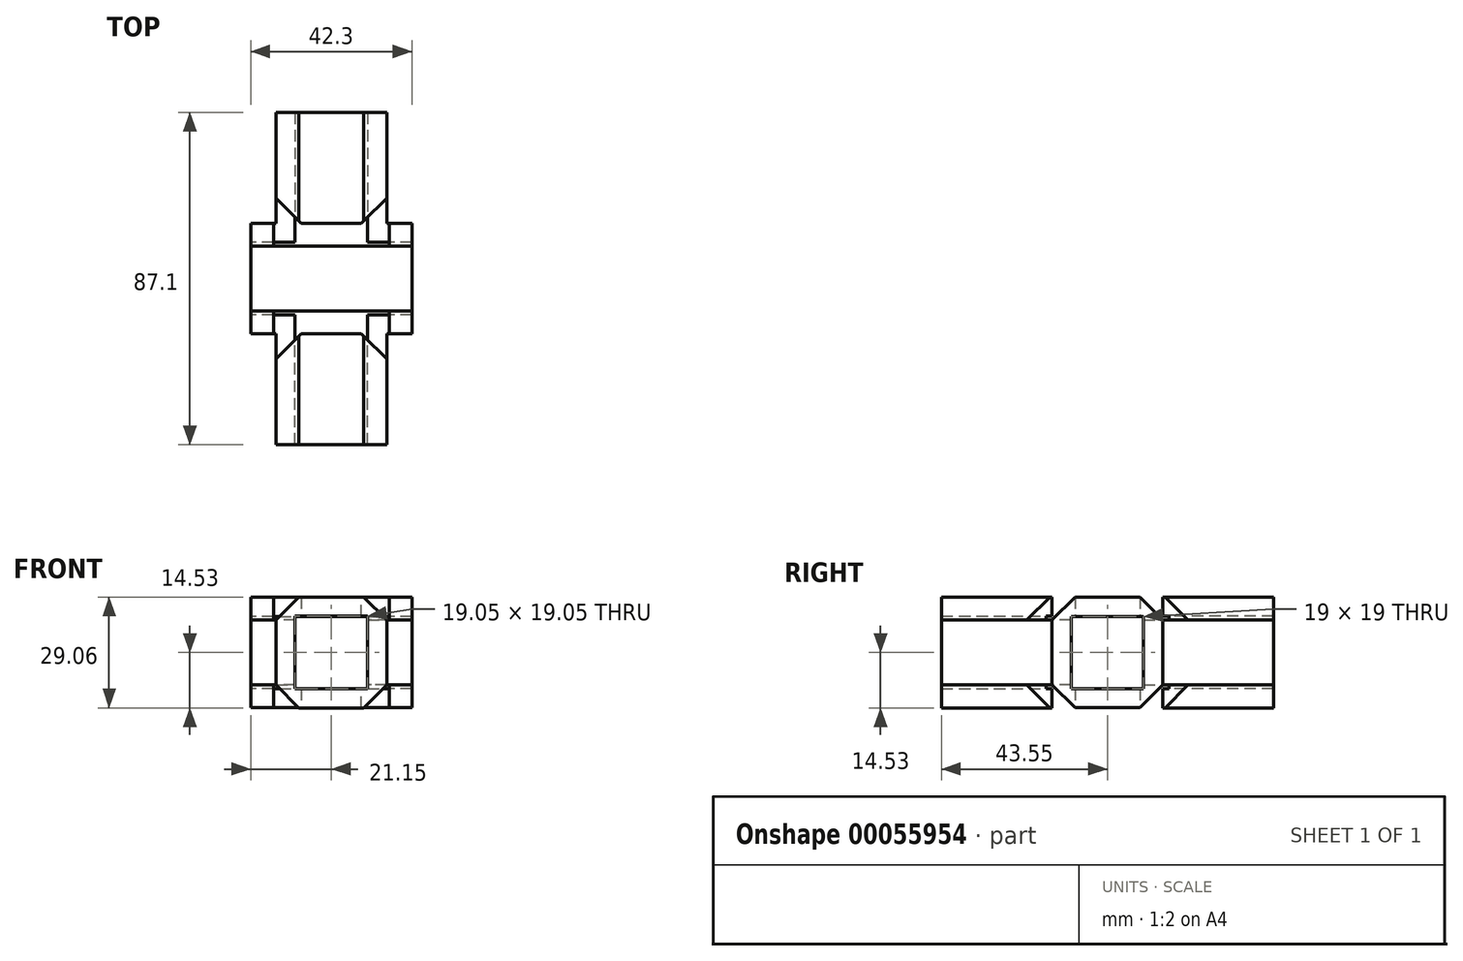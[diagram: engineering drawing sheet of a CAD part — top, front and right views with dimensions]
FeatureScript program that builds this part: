
annotation { "Feature Type Name" : "Feature", "Feature Type Description" : "" }
export const myFeature = defineFeature(function(context is Context, id is Id, definition is map)
    precondition{}
    {
        {
            var Q0;
            Q0=qCreatedBy(makeId("Right.planeOp"),FACE);
            var sketch = newSketch(context, id + "F0", { "sketchPlane" : qUnion([Q0])});
            skLineSegment(sketch, "E0.rect.bottom", {"start": v(9.5, 9.5) * mm, "end": v(0, 9.5) * mm});
            skLineSegment(sketch, "E0.rect.top", {"start": v(9.5, -9.5) * mm, "end": v(0, -9.5) * mm});
            skLineSegment(sketch, "E0.rect.left", {"start": v(9.5, 9.5) * mm, "end": v(9.5, -9.5) * mm});
            skPoint(sketch, "E0.rect.middle", {"position": v(0, 0) * mm});
            skLineSegment(sketch, "E1.rect.bottom", {"start": v(14.5, 14.5) * mm, "end": v(0, 14.5) * mm});
            skLineSegment(sketch, "E1.rect.top", {"start": v(14.5, -14.5) * mm, "end": v(0, -14.5) * mm});
            skLineSegment(sketch, "E1.rect.left", {"start": v(14.5, 14.5) * mm, "end": v(14.5, -14.5) * mm});
            skLineSegment(sketch, "E2", {"start": v(0, 9.5) * mm, "end": v(0, 14.5) * mm});
            skLineSegment(sketch, "E3", {"start": v(0, -9.5) * mm, "end": v(0, -14.5) * mm});
            skSolve(sketch);
        }
        {
            var Q0;
            Q0=makeQuery(id+"F0.imprint","IMPRINT",FACE,{"disambiguationData":[TD([[makeQuery(id+"F0.imprint","IMPRINT",EDGE,{"derivedFrom":sQuery(id+"F0.wireOp",EDGE,"5346ee42-6b44-4ab4-b06a-5ea702be0697.bottom")}),1.0]])]});
            var Q1;
            Q1=makeQuery(id+"F0.imprint","IMPRINT",FACE,{"disambiguationData":[TD([[makeQuery(id+"F0.imprint","IMPRINT",EDGE,{"derivedFrom":sQuery(id+"F0.wireOp",EDGE,"9599e187-f427-41b1-8912-62db417e26b9.bottom")}),1.0]])]});
            var Q2;
            Q2=makeQuery(id+"F0.imprint","IMPRINT",FACE,{"disambiguationData":[TD([[makeQuery(id+"F0.imprint","IMPRINT",EDGE,{"derivedFrom":sQuery(id+"F0.wireOp",EDGE,"E0.rect.bottom")}),-1.0]])]});
            extrude(context, id + "F1", {"entities" : qUnion([Q0, Q1, Q2]), "depth" : 42.3 * mm});
        }
        {
            var Q0;
            Q0=makeQuery(id+"F1.opExtrude","SWEPT_FACE",FACE,{"disambiguationData":[OSD([sQuery(id+"F0.wireOp",EDGE,"E1.rect.left")])]});
            var sketch = newSketch(context, id + "F2", { "sketchPlane" : qUnion([Q0])});
            skLineSegment(sketch, "E4.bottom", {"start": v(-42.3, 14.5) * mm, "end": v(-36.3, 14.5) * mm, "construction": true});
            skLineSegment(sketch, "E4.top", {"start": v(-42.3, 8.5) * mm, "end": v(-36.3, 8.5) * mm, "construction": true});
            skLineSegment(sketch, "E4.left", {"start": v(-42.3, 14.5) * mm, "end": v(-42.3, 8.5) * mm, "construction": true});
            skLineSegment(sketch, "E4.right", {"start": v(-36.3, 14.5) * mm, "end": v(-36.3, 8.5) * mm, "construction": true});
            skLineSegment(sketch, "E5.bottom", {"start": v(0, 14.5) * mm, "end": v(-6, 14.5) * mm, "construction": true});
            skLineSegment(sketch, "E5.top", {"start": v(0, 8.5) * mm, "end": v(-6, 8.5) * mm, "construction": true});
            skLineSegment(sketch, "E5.left", {"start": v(0, 14.5) * mm, "end": v(0, 8.5) * mm, "construction": true});
            skLineSegment(sketch, "E5.right", {"start": v(-6, 14.5) * mm, "end": v(-6, 8.5) * mm, "construction": true});
            skLineSegment(sketch, "E6.bottom", {"start": v(0, -14.5) * mm, "end": v(-6, -14.5) * mm, "construction": true});
            skLineSegment(sketch, "E6.top", {"start": v(0, -8.5) * mm, "end": v(-6, -8.5) * mm, "construction": true});
            skLineSegment(sketch, "E6.left", {"start": v(0, -14.5) * mm, "end": v(0, -8.5) * mm, "construction": true});
            skLineSegment(sketch, "E6.right", {"start": v(-6, -14.5) * mm, "end": v(-6, -8.5) * mm, "construction": true});
            skLineSegment(sketch, "E7.bottom", {"start": v(-42.3, -14.5) * mm, "end": v(-36.3, -14.5) * mm, "construction": true});
            skLineSegment(sketch, "E7.top", {"start": v(-42.3, -8.5) * mm, "end": v(-36.3, -8.5) * mm, "construction": true});
            skLineSegment(sketch, "E7.left", {"start": v(-42.3, -14.5) * mm, "end": v(-42.3, -8.5) * mm, "construction": true});
            skLineSegment(sketch, "E7.right", {"start": v(-36.3, -14.5) * mm, "end": v(-36.3, -8.5) * mm, "construction": true});
            skLineSegment(sketch, "E8.bottom", {"start": v(-36.3, 14.5) * mm, "end": v(-6, 14.5) * mm});
            skLineSegment(sketch, "E8.top", {"start": v(-36.3, 8.5) * mm, "end": v(-6, 8.5) * mm});
            skLineSegment(sketch, "E8.left", {"start": v(-36.3, 14.5) * mm, "end": v(-36.3, 8.5) * mm});
            skLineSegment(sketch, "E8.right", {"start": v(-6, 14.5) * mm, "end": v(-6, 8.5) * mm});
            skLineSegment(sketch, "E9.bottom", {"start": v(-36.3, -8.5) * mm, "end": v(-6, -8.5) * mm});
            skLineSegment(sketch, "E9.top", {"start": v(-36.3, -14.5) * mm, "end": v(-6, -14.5) * mm});
            skLineSegment(sketch, "E9.left", {"start": v(-36.3, -8.5) * mm, "end": v(-36.3, -14.5) * mm});
            skLineSegment(sketch, "E9.right", {"start": v(-6, -8.5) * mm, "end": v(-6, -14.5) * mm});
            skSolve(sketch);
        }
        {
            var Q0;
            Q0=makeQuery(id+"F2.imprint","IMPRINT",FACE,{"disambiguationData":[TD([[makeQuery(id+"F2.imprint","IMPRINT",EDGE,{"derivedFrom":sQuery(id+"F2.wireOp",EDGE,"E8.bottom")}),-1.0]])]});
            var Q1;
            Q1=makeQuery(id+"F2.imprint","IMPRINT",FACE,{"disambiguationData":[TD([[makeQuery(id+"F2.imprint","IMPRINT",EDGE,{"derivedFrom":sQuery(id+"F2.wireOp",EDGE,"E9.bottom")}),-1.0]])]});
            extrude(context, id + "F3", {"entities" : qUnion([Q0, Q1]), "operationType" : NewBodyOperationType.REMOVE, "oppositeDirection" : true, "depth" : 6 * mm});
        }
        {
            var Q0;
            {var subQ0=sQuery(id+"F0.wireOp",EDGE,"E1.rect.left");var subQ1=sQuery(id+"F0.wireOp",EDGE,"E1.rect.top");Q0=makeQuery(id+"F3.boolean.opBoolean","SPLIT",EDGE,{"disambiguationData":[TD([makeQuery(id+"F3.opExtrude","SWEPT_FACE",FACE,{"disambiguationData":[OSD([sQuery(id+"F2.wireOp",EDGE,"E9.right")])]})])],"derivedFrom":makeQuery(id+"F1.opExtrude","SWEPT_EDGE",EDGE,{"disambiguationData":[OSD([subQ1,subQ0])]})});}
            var Q1;
            {var subQ0=sQuery(id+"F0.wireOp",EDGE,"E1.rect.left");var subQ1=sQuery(id+"F0.wireOp",EDGE,"E1.rect.top");Q1=makeQuery(id+"F3.boolean.opBoolean","SPLIT",EDGE,{"disambiguationData":[TD([makeQuery(id+"F3.opExtrude","SWEPT_FACE",FACE,{"disambiguationData":[OSD([sQuery(id+"F2.wireOp",EDGE,"E9.left")])]})])],"derivedFrom":makeQuery(id+"F1.opExtrude","SWEPT_EDGE",EDGE,{"disambiguationData":[OSD([subQ1,subQ0])]})});}
            var Q2;
            {var subQ0=sQuery(id+"F0.wireOp",EDGE,"E1.rect.left");var subQ1=sQuery(id+"F0.wireOp",EDGE,"E1.rect.bottom");Q2=makeQuery(id+"F3.boolean.opBoolean","SPLIT",EDGE,{"disambiguationData":[TD([makeQuery(id+"F3.opExtrude","SWEPT_FACE",FACE,{"disambiguationData":[OSD([sQuery(id+"F2.wireOp",EDGE,"E8.left")])]})])],"derivedFrom":makeQuery(id+"F1.opExtrude","SWEPT_EDGE",EDGE,{"disambiguationData":[OSD([subQ1,subQ0])]})});}
            var Q3;
            {var subQ0=sQuery(id+"F0.wireOp",EDGE,"E1.rect.left");var subQ1=sQuery(id+"F0.wireOp",EDGE,"E1.rect.bottom");Q3=makeQuery(id+"F3.boolean.opBoolean","SPLIT",EDGE,{"disambiguationData":[TD([makeQuery(id+"F3.opExtrude","SWEPT_FACE",FACE,{"disambiguationData":[OSD([sQuery(id+"F2.wireOp",EDGE,"E8.right")])]})])],"derivedFrom":makeQuery(id+"F1.opExtrude","SWEPT_EDGE",EDGE,{"disambiguationData":[OSD([subQ1,subQ0])]})});}
            chamfer(context, id + "F4", {"entities" : qUnion([Q0, Q1, Q2, Q3]), "width" : 6 * mm, "tangentPropagation" : true});
        }
        {
            var Q0;
            Q0=makeQuery(id+"F1.opExtrude","SWEPT_FACE",FACE,{"disambiguationData":[OSD([sQuery(id+"F0.wireOp",EDGE,"E1.rect.left")])]});
            var sketch = newSketch(context, id + "F5", { "sketchPlane" : qUnion([Q0])});
            skLineSegment(sketch, "E10", {"start": v(-21.15, 9.5) * mm, "end": v(-21.15, -9.5) * mm, "construction": true});
            skLineSegment(sketch, "E11.rect.bottom", {"start": v(-11.62, 9.53) * mm, "end": v(-30.67, 9.53) * mm});
            skLineSegment(sketch, "E11.rect.top", {"start": v(-11.62, -9.52) * mm, "end": v(-30.67, -9.52) * mm});
            skLineSegment(sketch, "E11.rect.left", {"start": v(-11.62, 9.53) * mm, "end": v(-11.62, -9.52) * mm});
            skLineSegment(sketch, "E11.rect.right", {"start": v(-30.67, 9.53) * mm, "end": v(-30.67, -9.52) * mm});
            skPoint(sketch, "E11.rect.middle", {"position": v(-21.15, 0) * mm});
            skLineSegment(sketch, "E12.rect.bottom", {"start": v(-6.62, 14.53) * mm, "end": v(-35.67, 14.53) * mm});
            skLineSegment(sketch, "E12.rect.top", {"start": v(-6.62, -14.52) * mm, "end": v(-35.67, -14.52) * mm});
            skLineSegment(sketch, "E12.rect.left", {"start": v(-6.62, 14.53) * mm, "end": v(-6.62, -14.52) * mm});
            skLineSegment(sketch, "E12.rect.right", {"start": v(-35.67, 14.53) * mm, "end": v(-35.67, -14.53) * mm});
            skSolve(sketch);
        }
        {
            var Q0;
            {var subQ0=sQuery(id+"F5.wireOp",EDGE,"E11.rect.right");var subQ1=makeQuery(id+"F3.boolean.opBoolean","COPY",EDGE,{"derivedFrom":makeQuery(id+"F3.opExtrude","CAP_EDGE",EDGE,{"disambiguationData":[OSD([sQuery(id+"F2.wireOp",EDGE,"E8.top")])],"isStart":true})});var subQ2=makeQuery(id+"F5.imprint","INTERSECT",VERTEX,{"derivedFrom":[subQ1,subQ0]});Q0=makeQuery(id+"F5.imprint","IMPRINT",FACE,{"disambiguationData":[TD([[makeQuery(id+"F5.imprint","IMPRINT",EDGE,{"disambiguationData":[TD([[subQ2,-1.0]])],"derivedFrom":subQ0}),-1.0]])]});}
            var Q1;
            {var subQ0=sQuery(id+"F5.wireOp",EDGE,"E11.rect.left");var subQ1=makeQuery(id+"F3.boolean.opBoolean","COPY",EDGE,{"derivedFrom":makeQuery(id+"F3.opExtrude","CAP_EDGE",EDGE,{"disambiguationData":[OSD([sQuery(id+"F2.wireOp",EDGE,"E8.top")])],"isStart":true})});var subQ2=makeQuery(id+"F5.imprint","INTERSECT",VERTEX,{"derivedFrom":[subQ1,subQ0]});Q1=makeQuery(id+"F5.imprint","IMPRINT",FACE,{"disambiguationData":[TD([[makeQuery(id+"F5.imprint","IMPRINT",EDGE,{"disambiguationData":[TD([[subQ2,-1.0]])],"derivedFrom":subQ0}),1.0]])]});}
            var Q2;
            {var subQ1=sQuery(id+"F5.wireOp",EDGE,"E11.rect.bottom");Q2=makeQuery(id+"F5.imprint","IMPRINT",FACE,{"disambiguationData":[TD([[makeQuery(id+"F5.imprint","IMPRINT",EDGE,{"derivedFrom":subQ1}),-1.0]])]});}
            var Q3;
            {var subQ1=sQuery(id+"F5.wireOp",EDGE,"E11.rect.top");Q3=makeQuery(id+"F5.imprint","IMPRINT",FACE,{"disambiguationData":[TD([[makeQuery(id+"F5.imprint","IMPRINT",EDGE,{"derivedFrom":subQ1}),1.0]])]});}
            extrude(context, id + "F6", {"entities" : qUnion([Q0, Q1, Q2, Q3]), "operationType" : NewBodyOperationType.ADD, "depth" : 29.05 * mm});
        }
        {
            var Q0;
            {var subQ0=sQuery(id+"F5.wireOp",EDGE,"E11.rect.left");Q0=makeQuery(id+"F6.boolean.opBoolean","SPLIT",FACE,{"disambiguationData":[TD([makeQuery(id+"F6.opExtrude","SWEPT_FACE",FACE,{"disambiguationData":[OSD([subQ0])]})])],"derivedFrom":makeQuery(id+"F1.opExtrude","SWEPT_FACE",FACE,{"disambiguationData":[OSD([sQuery(id+"F0.wireOp",EDGE,"E1.rect.left")])]})});}
            extrude(context, id + "F7", {"entities" : qUnion([Q0]), "operationType" : NewBodyOperationType.REMOVE, "endBound" : BoundingType.UP_TO_NEXT, "oppositeDirection" : true, "depth" : 25 * mm});
        }
        {
            var Q0;
            {var subQ0=sQuery(id+"F5.wireOp",EDGE,"E12.rect.right");Q0=makeQuery(id+"F6.boolean.opBoolean","SPLIT",EDGE,{"disambiguationData":[topologyDisambiguationEdgeConnected([makeQuery(id+"F1.opExtrude","SWEPT_FACE",FACE,{"disambiguationData":[OSD([sQuery(id+"F0.wireOp",EDGE,"E1.rect.left")])]}),makeQuery(id+"F6.opExtrude","SWEPT_FACE",FACE,{"disambiguationData":[OSD([subQ0])]})])],"derivedFrom":makeQuery(id+"F6.opExtrude","CAP_EDGE",EDGE,{"disambiguationData":[OSD([subQ0])],"isStart":true})});}
            var Q1;
            {var subQ0=sQuery(id+"F5.wireOp",EDGE,"E12.rect.left");Q1=makeQuery(id+"F6.boolean.opBoolean","SPLIT",EDGE,{"disambiguationData":[topologyDisambiguationEdgeConnected([makeQuery(id+"F1.opExtrude","SWEPT_FACE",FACE,{"disambiguationData":[OSD([sQuery(id+"F0.wireOp",EDGE,"E1.rect.left")])]}),makeQuery(id+"F6.opExtrude","SWEPT_FACE",FACE,{"disambiguationData":[OSD([subQ0])]})])],"derivedFrom":makeQuery(id+"F6.opExtrude","CAP_EDGE",EDGE,{"disambiguationData":[OSD([subQ0])],"isStart":true})});}
            chamfer(context, id + "F8", {"entities" : qUnion([Q0, Q1]), "width" : 6.62 * mm, "tangentPropagation" : true});
        }
        {
            var Q0;
            Q0=makeQuery(id+"F6.opExtrude","SWEPT_EDGE",EDGE,{"disambiguationData":[OSD([sQuery(id+"F5.wireOp",EDGE,"E12.rect.bottom"),sQuery(id+"F5.wireOp",EDGE,"E12.rect.left")])]});
            var Q1;
            Q1=makeQuery(id+"F6.opExtrude","SWEPT_EDGE",EDGE,{"disambiguationData":[OSD([sQuery(id+"F5.wireOp",EDGE,"E12.rect.bottom"),sQuery(id+"F5.wireOp",EDGE,"E12.rect.right")])]});
            var Q2;
            Q2=makeQuery(id+"F6.opExtrude","SWEPT_EDGE",EDGE,{"disambiguationData":[OSD([sQuery(id+"F5.wireOp",EDGE,"E12.rect.top"),sQuery(id+"F5.wireOp",EDGE,"E12.rect.right")])]});
            var Q3;
            Q3=makeQuery(id+"F6.opExtrude","SWEPT_EDGE",EDGE,{"disambiguationData":[OSD([sQuery(id+"F5.wireOp",EDGE,"E12.rect.top"),sQuery(id+"F5.wireOp",EDGE,"E12.rect.left")])]});
            chamfer(context, id + "F9", {"entities" : qUnion([Q0, Q1, Q2, Q3]), "width" : 6 * mm, "tangentPropagation" : true});
        }
        {
            var Q0;
            Q0=makeQuery(id+"F1.opExtrude","SWEPT_FACE",FACE,{"disambiguationData":[OSD([sQuery(id+"F0.wireOp",EDGE,"E0.rect.top")])]});
            var sketch = newSketch(context, id + "F10", { "sketchPlane" : qUnion([Q0])});
            skLineSegment(sketch, "E13", {"start": v(6, 9.5) * mm, "end": v(36.3, 9.5) * mm, "construction": true});
            skSolve(sketch);
        }
        {
            var Q0;
            Q0=makeQuery(id+"F1.opExtrude","SWEPT_BODY",BODY,{"disambiguationData":[OSD([sQuery(id+"F0.wireOp",EDGE,"E0.rect.bottom"),sQuery(id+"F0.wireOp",EDGE,"E0.rect.top"),sQuery(id+"F0.wireOp",EDGE,"E0.rect.left"),sQuery(id+"F0.wireOp",EDGE,"E1.rect.bottom"),sQuery(id+"F0.wireOp",EDGE,"E1.rect.top"),sQuery(id+"F0.wireOp",EDGE,"E1.rect.left"),sQuery(id+"F0.wireOp",EDGE,"E2"),sQuery(id+"F0.wireOp",EDGE,"E3")])]});
            var Q1;
            Q1=makeQuery(id+"F1.opExtrude","SWEPT_FACE",FACE,{"disambiguationData":[OSD([sQuery(id+"F0.wireOp",EDGE,"E2")])]});
            mirror(context, id + "F11", {"operationType" : NewBodyOperationType.ADD, "entities" : qUnion([Q0]), "mirrorPlane" : qUnion([Q1])});
        }
    });
